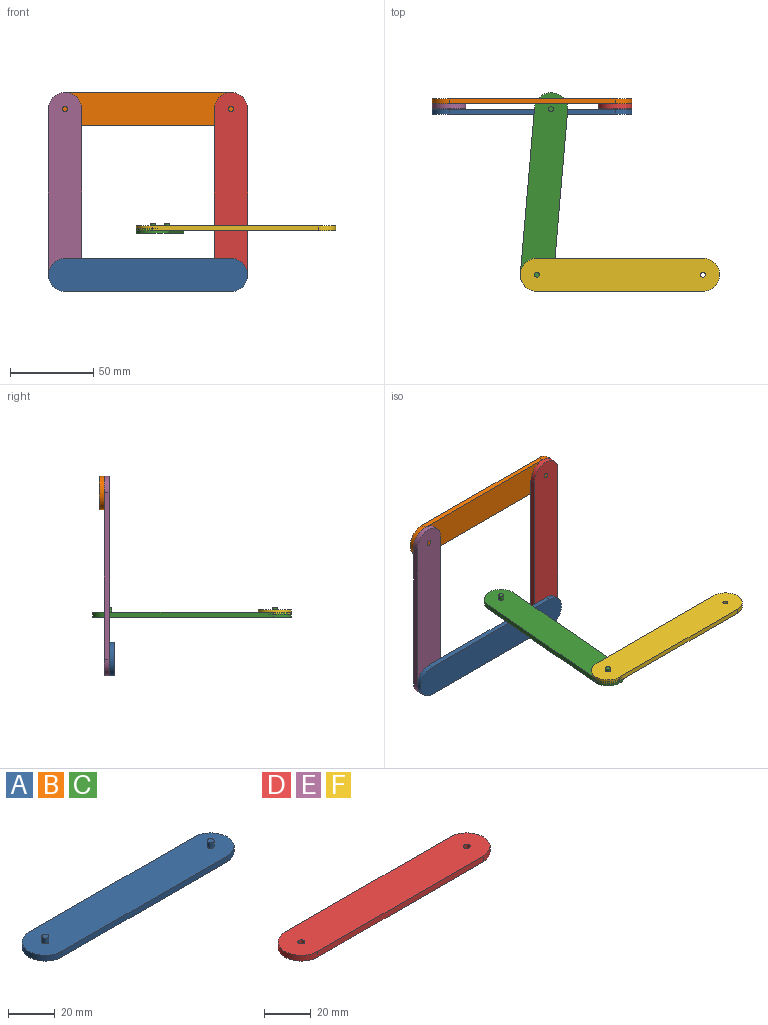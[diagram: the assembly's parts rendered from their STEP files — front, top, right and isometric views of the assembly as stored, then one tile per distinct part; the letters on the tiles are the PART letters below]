
ASSEMBLY  parts=6 mates=5
PART A: 10 faces, bbox 120x20x6 mm
  f0: cylinder r=10mm len=20mm, axis (0,0,-1), area 94.2mm2, adj f1,f3,f4,f5
  f1: plane 100x3mm, normal (0,1,0), area 300mm2, adj f0,f2,f4,f5
  f2: cylinder r=10mm len=20mm, axis (0,0,-1), area 94.2mm2, adj f1,f3,f4,f5
  f3: plane 100x3mm, normal (0,-1,0), area 300mm2, adj f0,f2,f4,f5
  f4: plane 120x20mm, normal (0,0,1), area 2300mm2, adj f0,f1,f2,f3,f6,f8
  f5: plane 120x20mm, normal (0,0,-1), area 2314.2mm2, adj f0,f1,f2,f3
  f6: cylinder r=1.5mm len=3mm, axis (0,0,-1), area 28.3mm2, adj f4,f7
  f7: plane 3x3mm, normal (0,0,1), area 7.1mm2, adj f6
  f8: cylinder r=1.5mm len=3mm, axis (0,0,-1), area 28.3mm2, adj f4,f9
  f9: plane 3x3mm, normal (0,0,1), area 7.1mm2, adj f8
PART B: same geometry as A
PART C: same geometry as A
PART D: 8 faces, bbox 120x20x3 mm
  f0: cylinder r=10mm len=20mm, axis (0,0,-1), area 94.2mm2, adj f1,f3,f4,f5
  f1: plane 100x3mm, normal (0,1,0), area 300mm2, adj f0,f2,f4,f5
  f2: cylinder r=10mm len=20mm, axis (0,0,-1), area 94.2mm2, adj f1,f3,f4,f5
  f3: plane 100x3mm, normal (0,-1,0), area 300mm2, adj f0,f2,f4,f5
  f4: plane 120x20mm, normal (0,0,1), area 2300mm2, adj f0,f1,f2,f3,f6,f7
  f5: plane 120x20mm, normal (0,0,-1), area 2300mm2, adj f0,f1,f2,f3,f6,f7
  f6: cylinder r=1.5mm len=3mm, axis (0,0,1), area 28.3mm2, adj f4,f5
  f7: cylinder r=1.5mm len=3mm, axis (0,0,1), area 28.3mm2, adj f4,f5
PART E: same geometry as D
PART F: same geometry as D
PLACE A rot(axis=(-1,0,0),90deg) t=(-26.03,-14.67,-91.87)mm
PLACE B rot(axis=(1,0,0),90deg) t=(-26.03,-5.67,8.13)mm fixed
PLACE C rot(axis=(0,0,1),85.1deg) t=(-18.82,-61.58,-66.76)mm
PLACE D rot(axis=(0.58,0.58,-0.58),120deg) t=(23.97,-8.67,-41.87)mm
PLACE E rot(axis=(0.58,0.58,-0.58),120deg) t=(-76.03,-8.67,-41.87)mm
PLACE F t=(26.91,-111.4,-65.26)mm fixed
MATE revolute E.f2 <-> B.f8  axis (0,-1,0) through (-76.03,-11.67,8.13)mm
MATE revolute D.f2 <-> B.f6  axis (0,-1,0) through (23.97,-11.67,8.13)mm
MATE revolute C.f8 <-> F.f7  axis (0,0,-1) through (-23.09,-111.4,-62.26)mm
MATE revolute A.f6 <-> D.f0  axis (0,1,0) through (23.97,-8.67,-91.87)mm
MATE revolute A.f8 <-> E.f0  axis (0,1,0) through (-76.03,-8.67,-91.87)mm
